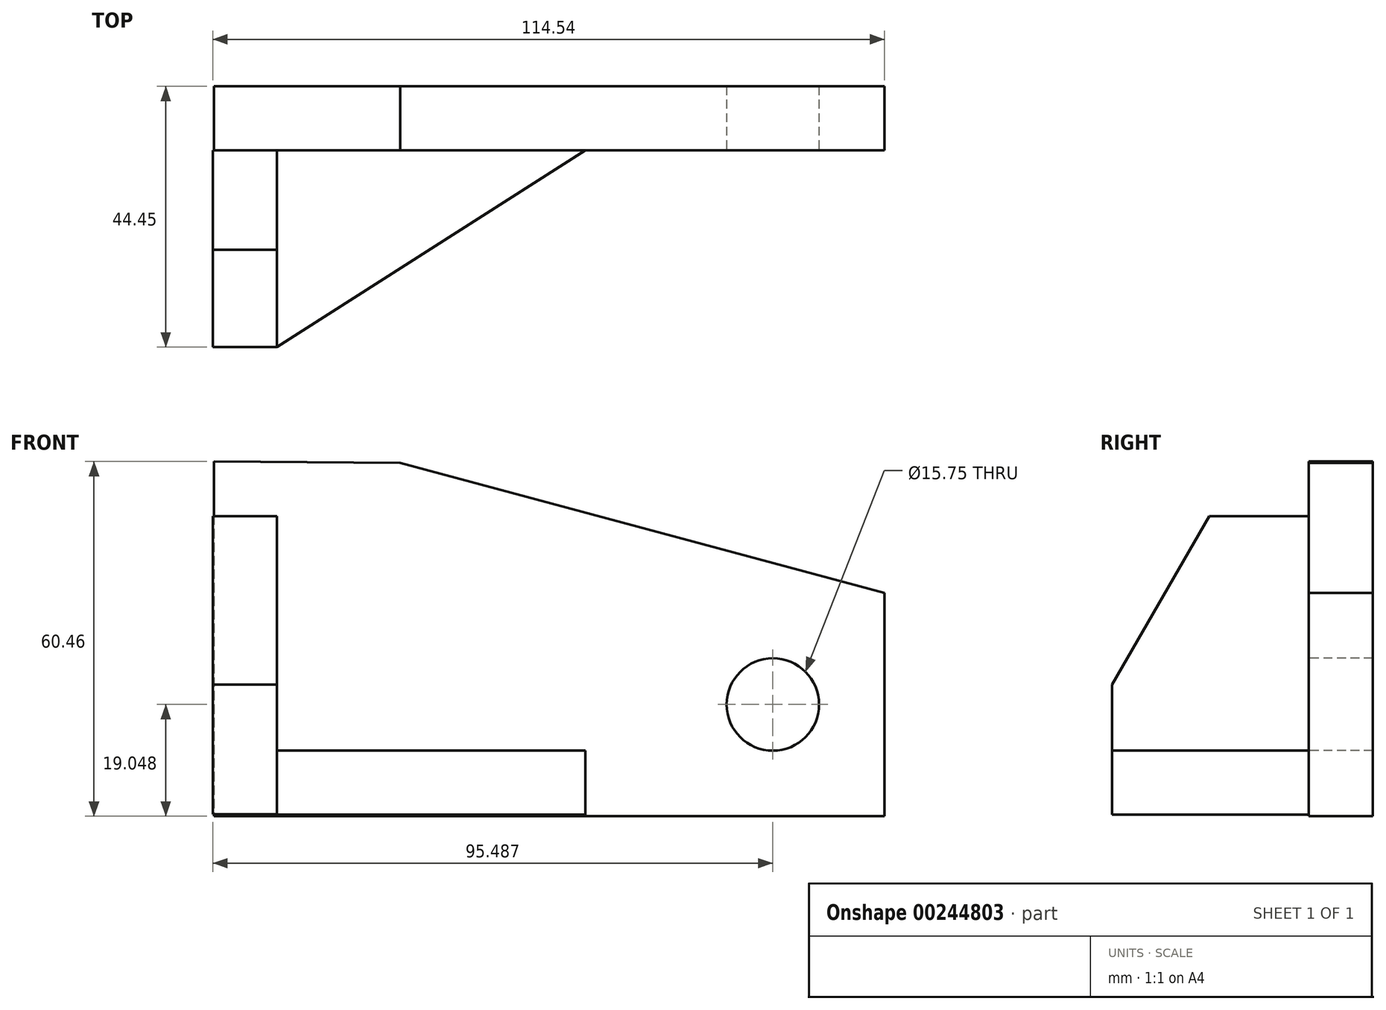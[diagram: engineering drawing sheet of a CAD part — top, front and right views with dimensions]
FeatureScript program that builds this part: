
annotation { "Feature Type Name" : "Feature", "Feature Type Description" : "" }
export const myFeature = defineFeature(function(context is Context, id is Id, definition is map)
    precondition{}
    {
        {
            var Q0;
            Q0=qCreatedBy(makeId("Front.planeOp"),FACE);
            var sketch = newSketch(context, id + "F0", { "sketchPlane" : qUnion([Q0])});
            skLineSegment(sketch, "E0", {"start": v(0.24, 60.15) * mm, "end": v(0.24, -0.31) * mm});
            skLineSegment(sketch, "E1", {"start": v(0.24, -0.31) * mm, "end": v(114.54, -0.31) * mm});
            skLineSegment(sketch, "E2", {"start": v(114.54, -0.31) * mm, "end": v(114.54, 37.77) * mm});
            skLineSegment(sketch, "E3", {"start": v(114.54, 37.77) * mm, "end": v(31.99, 59.89) * mm});
            skLineSegment(sketch, "E4", {"start": v(31.99, 59.89) * mm, "end": v(0.24, 60.15) * mm});
            skLineSegment(sketch, "E5", {"start": v(31.99, 59.89) * mm, "end": v(114.54, 59.89) * mm, "construction": true});
            skLineSegment(sketch, "E6", {"start": v(114.54, 59.89) * mm, "end": v(114.54, 37.77) * mm, "construction": true});
            skCircle(sketch, "E7", {"center": v(95.49, 18.74) * mm, "radius": 7.87 * mm});
            skSolve(sketch);
        }
        {
            var Q0;
            Q0=qCreatedBy(makeId("Right.planeOp"),FACE);
            var sketch = newSketch(context, id + "F1", { "sketchPlane" : qUnion([Q0])});
            skLineSegment(sketch, "E8", {"start": v(0, 50.84) * mm, "end": v(-16.96, 50.84) * mm});
            skLineSegment(sketch, "E9", {"start": v(-16.96, 50.84) * mm, "end": v(-33.53, 22.14) * mm});
            skLineSegment(sketch, "E10", {"start": v(-33.53, 22.14) * mm, "end": v(-33.53, 0.04) * mm});
            skLineSegment(sketch, "E11", {"start": v(-33.53, 0.04) * mm, "end": v(0, 0.04) * mm});
            skLineSegment(sketch, "E12", {"start": v(-33.53, 50.84) * mm, "end": v(-16.96, 50.84) * mm, "construction": true});
            skLineSegment(sketch, "E13", {"start": v(-33.53, 50.84) * mm, "end": v(-33.53, 22.14) * mm, "construction": true});
            skLineSegment(sketch, "E14", {"start": v(0, 50.84) * mm, "end": v(0, 0.04) * mm});
            skSolve(sketch);
        }
        {
            var Q0;
            Q0=qCreatedBy(makeId("Top.planeOp"),FACE);
            var sketch = newSketch(context, id + "F2", { "sketchPlane" : qUnion([Q0])});
            skLineSegment(sketch, "E15", {"start": v(0, 0) * mm, "end": v(0, -33.53) * mm, "construction": true});
            skLineSegment(sketch, "E16", {"start": v(0, -33.53) * mm, "end": v(10.92, -33.53) * mm, "construction": true});
            skLineSegment(sketch, "E17", {"start": v(10.92, -33.53) * mm, "end": v(10.92, 0) * mm});
            skLineSegment(sketch, "E18", {"start": v(10.92, 0) * mm, "end": v(63.5, 0) * mm});
            skLineSegment(sketch, "E19", {"start": v(63.5, 0) * mm, "end": v(10.92, -33.53) * mm});
            skLineSegment(sketch, "E20", {"start": v(63.5, -33.53) * mm, "end": v(63.5, 0) * mm, "construction": true});
            skLineSegment(sketch, "E21", {"start": v(10.92, -33.53) * mm, "end": v(63.5, -33.53) * mm, "construction": true});
            skSolve(sketch);
        }
        {
            var Q0;
            Q0=makeQuery(id+"F0.imprint","IMPRINT",FACE,{"disambiguationData":[TD([[makeQuery(id+"F0.imprint","IMPRINT",EDGE,{"derivedFrom":sQuery(id+"F0.wireOp",EDGE,"E0")}),1.0]])]});
            var Q1;
            {var subQ1=sQuery(id+"F0.wireOp",EDGE,"19825d30-e13e-486d-a56c-d66a0ac0c49d.top");Q1=makeQuery(id+"F0.imprint","IMPRINT",FACE,{"disambiguationData":[TD([[makeQuery(id+"F0.imprint","IMPRINT",EDGE,{"derivedFrom":subQ1}),1.0]])]});}
            extrude(context, id + "F3", {"entities" : qUnion([Q0, Q1]), "oppositeDirection" : true, "depth" : 10.92 * mm});
        }
        {
            var Q0;
            Q0=makeQuery(id+"F1.imprint","IMPRINT",FACE,{"disambiguationData":[TD([[makeQuery(id+"F1.imprint","IMPRINT",EDGE,{"derivedFrom":sQuery(id+"F1.wireOp",EDGE,"E8")}),1.0]])]});
            extrude(context, id + "F4", {"entities" : qUnion([Q0]), "operationType" : NewBodyOperationType.ADD, "depth" : 10.92 * mm});
        }
        {
            var Q0;
            Q0=makeQuery(id+"F2.imprint","IMPRINT",FACE,{"disambiguationData":[TD([[makeQuery(id+"F2.imprint","IMPRINT",EDGE,{"derivedFrom":sQuery(id+"F2.wireOp",EDGE,"E17")}),-1.0]])]});
            extrude(context, id + "F5", {"entities" : qUnion([Q0]), "operationType" : NewBodyOperationType.ADD, "depth" : 10.92 * mm});
        }
    });
